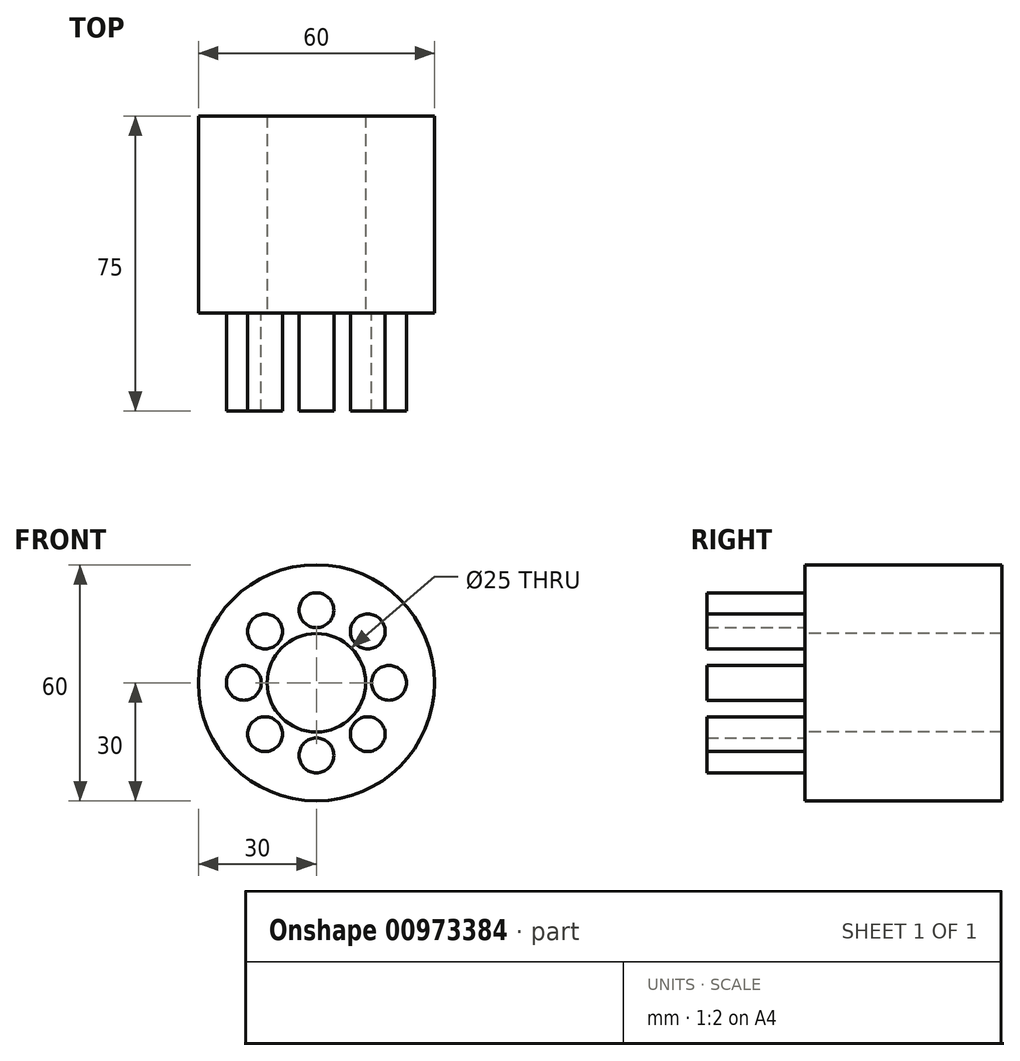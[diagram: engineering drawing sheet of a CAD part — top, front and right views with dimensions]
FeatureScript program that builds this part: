
annotation { "Feature Type Name" : "Feature", "Feature Type Description" : "" }
export const myFeature = defineFeature(function(context is Context, id is Id, definition is map)
    precondition{}
    {
        {
            var Q0;
            Q0=qCreatedBy(makeId("Front.planeOp"),FACE);
            var sketch = newSketch(context, id + "F0", { "sketchPlane" : qUnion([Q0])});
            skCircle(sketch, "E0", {"center": v(0, 0) * mm, "radius": 30 * mm});
            skSolve(sketch);
        }
        {
            var Q0;
            Q0 = qSketchRegion(id + "F0", true);
            extrude(context, id + "F1", {"entities" : qUnion([Q0]), "depth" : 50 * mm, "offsetDistance" : 25 * mm});
        }
        {
            var Q0;
            Q0=makeQuery(id+"F1.opExtrude","CAP_FACE",FACE,{"disambiguationData":[OSD([sQuery(id+"F0.wireOp",EDGE,"E0")])],"isStart":false});
            var sketch = newSketch(context, id + "F2", { "sketchPlane" : qUnion([Q0])});
            skCircle(sketch, "E1", {"center": v(0, 0) * mm, "radius": 12.5 * mm});
            skSolve(sketch);
        }
        {
            var Q0;
            Q0=makeQuery(id+"F2.imprint","IMPRINT",FACE,{"disambiguationData":[TD([[makeQuery(id+"F2.imprint","IMPRINT",EDGE,{"derivedFrom":sQuery(id+"F2.wireOp",EDGE,"E1")}),1.0]])]});
            extrude(context, id + "F3", {"entities" : qUnion([Q0]), "operationType" : NewBodyOperationType.REMOVE, "endBound" : BoundingType.THROUGH_ALL, "oppositeDirection" : true, "depth" : 25 * mm, "offsetDistance" : 25 * mm});
        }
        {
            var Q0;
            Q0=makeQuery(id+"F1.opExtrude","CAP_FACE",FACE,{"disambiguationData":[OSD([sQuery(id+"F0.wireOp",EDGE,"E0")])],"isStart":false});
            var sketch = newSketch(context, id + "F4", { "sketchPlane" : qUnion([Q0])});
            skCircle(sketch, "E2", {"center": v(18.44, 0) * mm, "radius": 4.42 * mm});
            skCircle(sketch, "E3.1.0", {"center": v(13.04, 13.04) * mm, "radius": 4.42 * mm});
            skCircle(sketch, "E3.2.0", {"center": v(0, 18.44) * mm, "radius": 4.42 * mm});
            skCircle(sketch, "E3.3.0", {"center": v(-13.04, 13.04) * mm, "radius": 4.42 * mm});
            skCircle(sketch, "E3.4.0", {"center": v(-18.44, 0) * mm, "radius": 4.42 * mm});
            skCircle(sketch, "E3.5.0", {"center": v(-13.04, -13.04) * mm, "radius": 4.42 * mm});
            skCircle(sketch, "E3.6.0", {"center": v(0, -18.44) * mm, "radius": 4.42 * mm});
            skCircle(sketch, "E3.7.0", {"center": v(13.04, -13.04) * mm, "radius": 4.42 * mm});
            skPoint(sketch, "E3.center", {"position": v(0, 0) * mm});
            skSolve(sketch);
        }
        {
            var Q0;
            Q0 = qSketchRegion(id + "F4", true);
            extrude(context, id + "F5", {"entities" : qUnion([Q0]), "operationType" : NewBodyOperationType.ADD, "depth" : 25 * mm, "offsetDistance" : 25 * mm});
        }
    });
